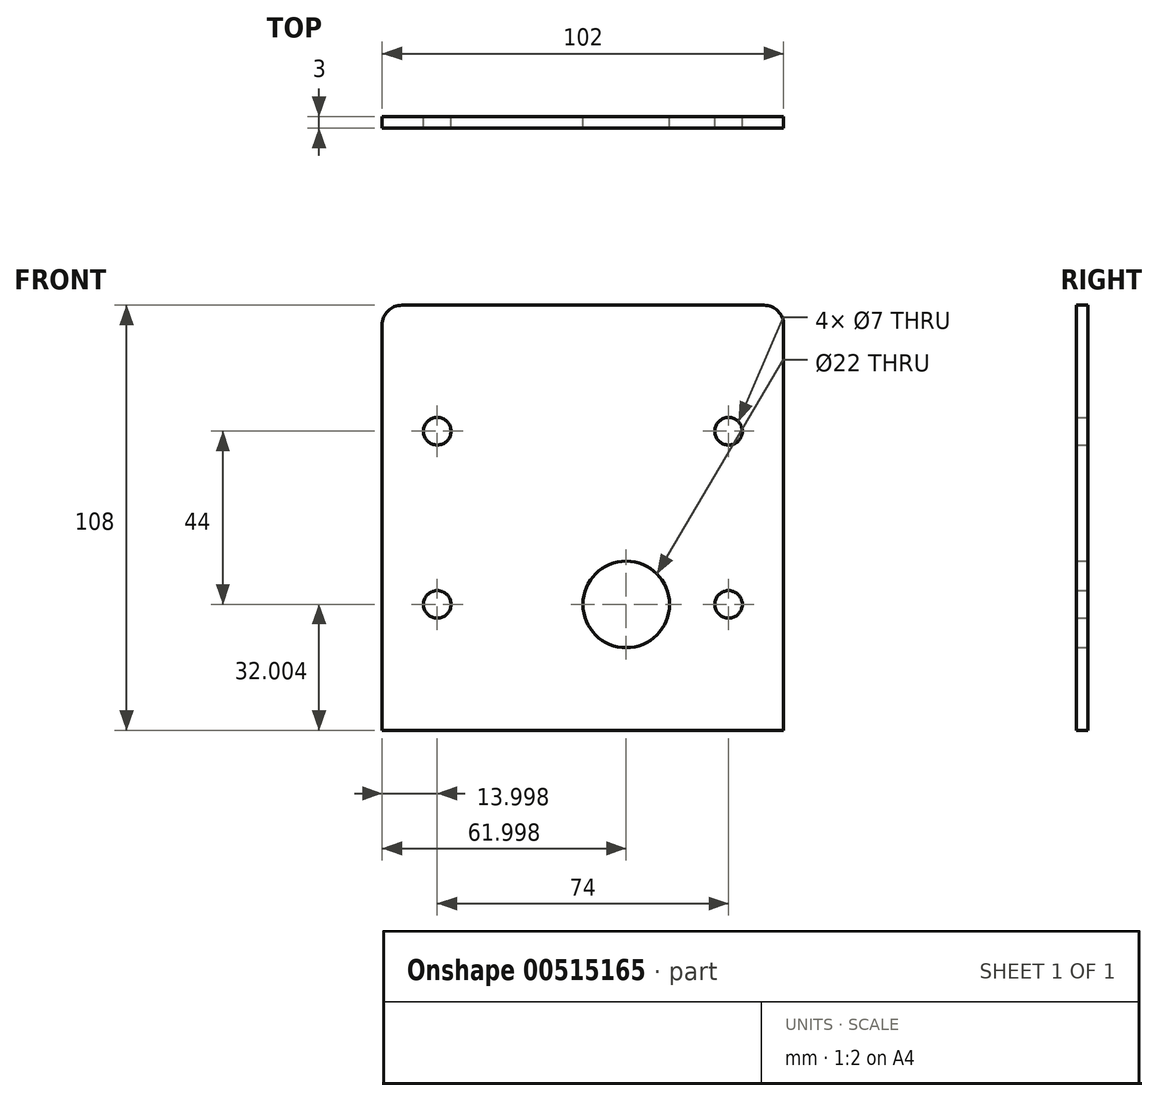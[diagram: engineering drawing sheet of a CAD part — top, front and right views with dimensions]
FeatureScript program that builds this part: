
annotation { "Feature Type Name" : "Feature", "Feature Type Description" : "" }
export const myFeature = defineFeature(function(context is Context, id is Id, definition is map)
    precondition{}
    {
        {
            var Q0;
            Q0=qCreatedBy(makeId("Front.planeOp"),FACE);
            var sketch = newSketch(context, id + "F0", { "sketchPlane" : qUnion([Q0])});
            skLineSegment(sketch, "E0", {"start": v(49.78, -51.56) * mm, "end": v(49.78, 56.44) * mm});
            skLineSegment(sketch, "E1", {"start": v(49.78, 56.44) * mm, "end": v(-52.22, 56.44) * mm});
            skLineSegment(sketch, "E2", {"start": v(-52.22, 56.44) * mm, "end": v(-52.22, -51.56) * mm});
            skLineSegment(sketch, "E3", {"start": v(-52.22, -51.56) * mm, "end": v(49.78, -51.56) * mm});
            skCircle(sketch, "E4", {"center": v(-38.22, 24.44) * mm, "radius": 3.5 * mm});
            skCircle(sketch, "E5", {"center": v(35.78, 24.44) * mm, "radius": 3.5 * mm});
            skCircle(sketch, "E6", {"center": v(35.78, -19.56) * mm, "radius": 3.5 * mm});
            skCircle(sketch, "E7", {"center": v(-38.22, -19.56) * mm, "radius": 3.5 * mm});
            skCircle(sketch, "E8", {"center": v(9.78, -19.56) * mm, "radius": 11 * mm});
            skSolve(sketch);
        }
        {
            var Q0;
            Q0 = qSketchRegion(id + "F0", true);
            extrude(context, id + "F1", {"entities" : qUnion([Q0]), "depth" : 3 * mm, "offsetDistance" : 25 * mm});
        }
        {
            var Q0;
            Q0=makeQuery(id+"F1.opExtrude","SWEPT_EDGE",EDGE,{"disambiguationData":[OSD([sQuery(id+"F0.wireOp",EDGE,"E0"),sQuery(id+"F0.wireOp",EDGE,"E1")])]});
            var Q1;
            Q1=makeQuery(id+"F1.opExtrude","SWEPT_EDGE",EDGE,{"disambiguationData":[OSD([sQuery(id+"F0.wireOp",EDGE,"E1"),sQuery(id+"F0.wireOp",EDGE,"E2")])]});
            fillet(context, id + "F2", {"entities" : qUnion([Q0, Q1]), "radius" : 5 * mm, "tangentPropagation" : true, "allowEdgeOverflow" : false});
        }
    });
